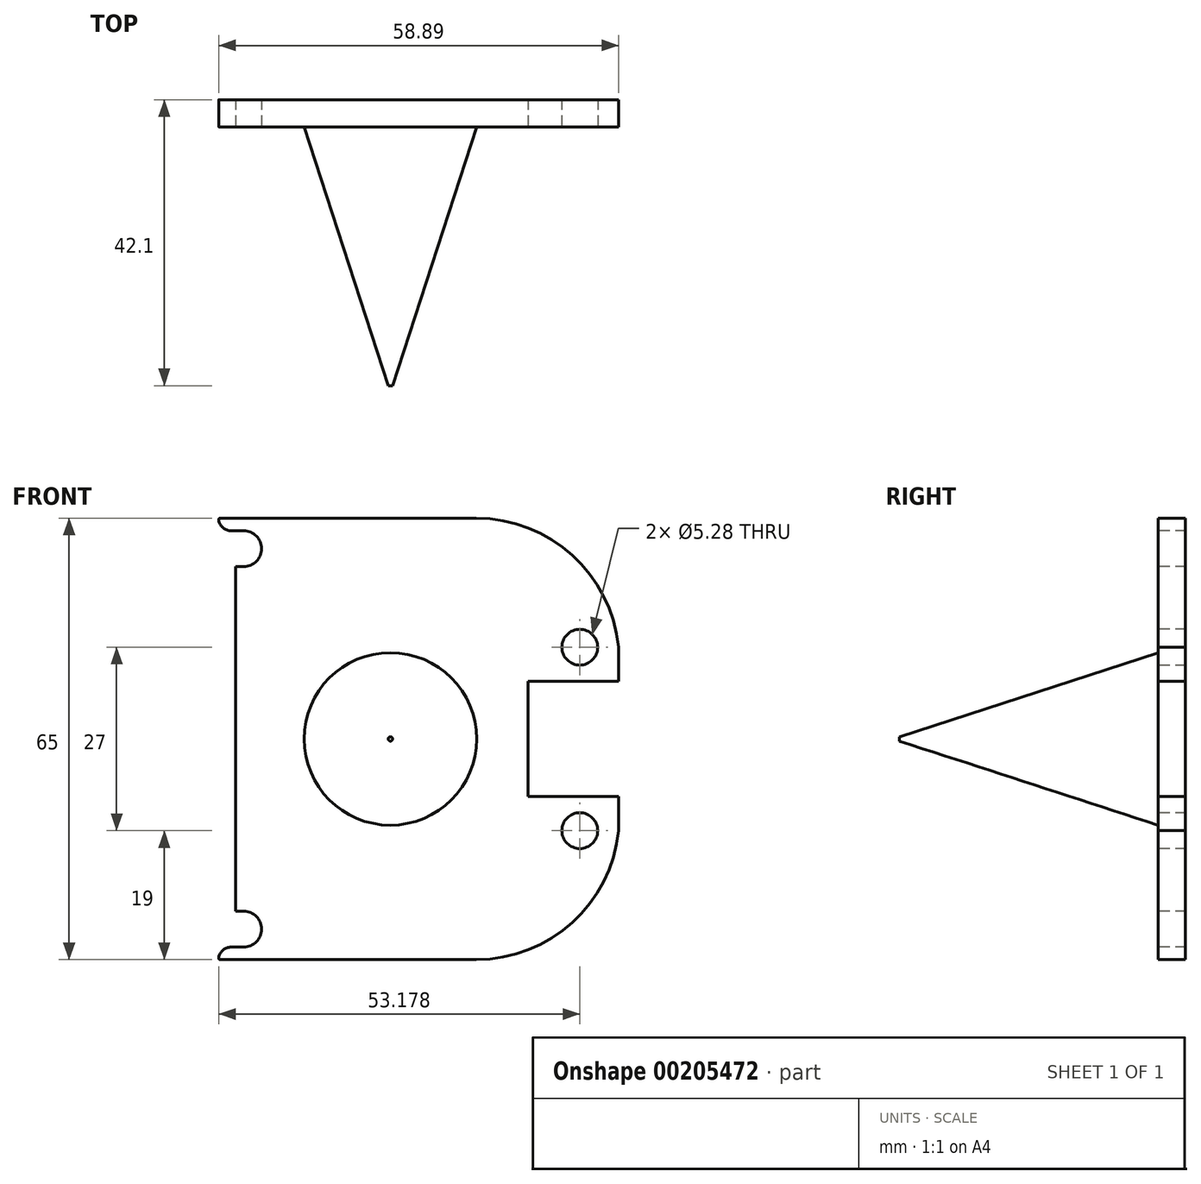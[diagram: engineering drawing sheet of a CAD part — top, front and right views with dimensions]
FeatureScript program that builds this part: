
annotation { "Feature Type Name" : "Feature", "Feature Type Description" : "" }
export const myFeature = defineFeature(function(context is Context, id is Id, definition is map)
    precondition{}
    {
        {
            var Q0;
            Q0=qCreatedBy(makeId("Front.planeOp"),FACE);
            var sketch = newSketch(context, id + "F0", { "sketchPlane" : qUnion([Q0])});
            skLineSegment(sketch, "E0.bottom", {"start": v(34.26, 37.43) * mm, "end": v(-34.26, 37.43) * mm});
            skLineSegment(sketch, "E0.top", {"start": v(34.26, -37.43) * mm, "end": v(-34.26, -37.43) * mm});
            skLineSegment(sketch, "E0.left", {"start": v(34.26, 37.43) * mm, "end": v(34.26, -37.43) * mm});
            skLineSegment(sketch, "E0.right", {"start": v(-34.26, 37.43) * mm, "end": v(-34.26, -37.43) * mm});
            skPoint(sketch, "E0.middle", {"position": v(0, 0) * mm});
            skSolve(sketch);
        }
        {
            var Q0;
            Q0=makeQuery(id+"F0.imprint","IMPRINT",FACE,{"disambiguationData":[TD([[makeQuery(id+"F0.imprint","IMPRINT",EDGE,{"derivedFrom":sQuery(id+"F0.wireOp",EDGE,"E0.bottom")}),1.0]])]});
            extrude(context, id + "F1", {"entities" : qUnion([Q0]), "depth" : 4 * mm});
        }
        {
            var Q0;
            Q0=makeQuery(id+"F1.opExtrude","CAP_FACE",FACE,{"disambiguationData":[OSD([sQuery(id+"F0.wireOp",EDGE,"E0.bottom"),sQuery(id+"F0.wireOp",EDGE,"E0.top"),sQuery(id+"F0.wireOp",EDGE,"E0.left"),sQuery(id+"F0.wireOp",EDGE,"E0.right")])],"isStart":false});
            var sketch = newSketch(context, id + "F2", { "sketchPlane" : qUnion([Q0])});
            skCircle(sketch, "E1", {"center": v(-34.26, 28) * mm, "radius": 2.64 * mm});
            skCircle(sketch, "E2", {"center": v(15.24, 13.5) * mm, "radius": 2.64 * mm});
            skLineSegment(sketch, "E3", {"start": v(-34.26, 0) * mm, "end": v(34.26, 0) * mm, "construction": true});
            skCircle(sketch, "E4.MirrorC", {"center": v(-34.26, -28) * mm, "radius": 2.64 * mm});
            skCircle(sketch, "E5.MirrorC", {"center": v(15.24, -13.5) * mm, "radius": 2.64 * mm});
            skLineSegment(sketch, "E6.bottom", {"start": v(7.64, 8.5) * mm, "end": v(20.95, 8.5) * mm});
            skLineSegment(sketch, "E7", {"start": v(-34.26, 32.5) * mm, "end": v(0, 32.5) * mm});
            skArc(sketch, "E8", {"start": v(0, 32.5) * mm, "mid": v(14.14, 27.04) * mm, "end": v(20.95, 13.5) * mm});
            skPoint(sketch, "E8.endSnap0", {"position": v(20.95, 8.5) * mm});
            skLineSegment(sketch, "E9", {"start": v(20.95, 13.5) * mm, "end": v(20.95, 8.5) * mm});
            skLineSegment(sketch, "E10", {"start": v(-34.26, 32.5) * mm, "end": v(-34.26, 37.43) * mm});
            skLineSegment(sketch, "E11", {"start": v(-34.26, 37.43) * mm, "end": v(34.26, 37.43) * mm});
            skLineSegment(sketch, "E12", {"start": v(34.26, 37.43) * mm, "end": v(34.26, 8.5) * mm});
            skLineSegment(sketch, "E13", {"start": v(7.64, 8.5) * mm, "end": v(7.64, 0) * mm});
            skLineSegment(sketch, "E14", {"start": v(7.64, 0) * mm, "end": v(34.26, 0) * mm});
            skLineSegment(sketch, "E15", {"start": v(34.26, 8.5) * mm, "end": v(34.26, 0) * mm});
            skLineSegment(sketch, "E16.MirrorCS", {"start": v(7.64, -8.5) * mm, "end": v(7.64, 0) * mm});
            skLineSegment(sketch, "E17.MirrorCS", {"start": v(7.64, -8.5) * mm, "end": v(20.95, -8.5) * mm});
            skLineSegment(sketch, "E18.MirrorCS", {"start": v(20.95, -13.5) * mm, "end": v(20.95, -8.5) * mm});
            skArc(sketch, "E19.MirrorCS", {"start": v(0, -32.5) * mm, "mid": v(14.14, -27.04) * mm, "end": v(20.95, -13.5) * mm});
            skLineSegment(sketch, "E20.MirrorCS", {"start": v(-34.26, -32.5) * mm, "end": v(0, -32.5) * mm});
            skLineSegment(sketch, "E21.MirrorCS", {"start": v(-34.26, -32.5) * mm, "end": v(-34.26, -37.43) * mm});
            skLineSegment(sketch, "E22.MirrorCS", {"start": v(-34.26, -37.43) * mm, "end": v(34.26, -37.43) * mm});
            skLineSegment(sketch, "E23.MirrorCS", {"start": v(34.26, -37.43) * mm, "end": v(34.26, -8.5) * mm});
            skLineSegment(sketch, "E24.MirrorCS", {"start": v(34.26, -8.5) * mm, "end": v(34.26, 0) * mm});
            skSolve(sketch);
        }
        {
            var Q0;
            Q0=qSketchRegion(id+"F2",true);
            extrude(context, id + "F3", {"entities" : qUnion([Q0]), "operationType" : NewBodyOperationType.REMOVE, "endBound" : BoundingType.THROUGH_ALL, "oppositeDirection" : true, "depth" : 25.4 * mm});
        }
        {
            var Q0;
            Q0=makeQuery(id+"F1.opExtrude","CAP_FACE",FACE,{"disambiguationData":[OSD([sQuery(id+"F0.wireOp",EDGE,"E0.bottom"),sQuery(id+"F0.wireOp",EDGE,"E0.top"),sQuery(id+"F0.wireOp",EDGE,"E0.left"),sQuery(id+"F0.wireOp",EDGE,"E0.right")])],"isStart":false});
            var sketch = newSketch(context, id + "F4", { "sketchPlane" : qUnion([Q0])});
            skLineSegment(sketch, "E25.bottom", {"start": v(-34.26, 25.36) * mm, "end": v(-35.46, 25.36) * mm});
            skLineSegment(sketch, "E25.top", {"start": v(-34.26, -25.36) * mm, "end": v(-35.46, -25.36) * mm});
            skLineSegment(sketch, "E25.left", {"start": v(-34.26, 25.36) * mm, "end": v(-34.26, -25.36) * mm});
            skLineSegment(sketch, "E25.right", {"start": v(-35.46, 25.36) * mm, "end": v(-35.46, -25.36) * mm});
            skLineSegment(sketch, "E26", {"start": v(-34.26, 30.64) * mm, "end": v(-36.06, 30.64) * mm});
            skArc(sketch, "E27", {"start": v(-36.06, 30.64) * mm, "mid": v(-37.4, 31.18) * mm, "end": v(-37.97, 32.5) * mm});
            skLineSegment(sketch, "E28", {"start": v(-37.97, 32.5) * mm, "end": v(-34.26, 32.5) * mm});
            skLineSegment(sketch, "E29", {"start": v(-35.46, 0) * mm, "end": v(0, 0) * mm, "construction": true});
            skArc(sketch, "E30.MirrorCS", {"start": v(-36.06, -30.64) * mm, "mid": v(-37.4, -31.18) * mm, "end": v(-37.97, -32.5) * mm});
            skLineSegment(sketch, "E31.MirrorCS", {"start": v(-34.26, -30.64) * mm, "end": v(-36.06, -30.64) * mm});
            skLineSegment(sketch, "E32.MirrorCS", {"start": v(-37.97, -32.5) * mm, "end": v(-34.26, -32.5) * mm});
            skSolve(sketch);
        }
        {
            var Q0;
            Q0=makeQuery(id+"F4.imprint","IMPRINT",FACE,{"disambiguationData":[TD([[makeQuery(id+"F4.imprint","IMPRINT",EDGE,{"derivedFrom":sQuery(id+"F4.wireOp",EDGE,"E30.MirrorCS")}),1.0]])]});
            var Q1;
            Q1=makeQuery(id+"F4.imprint","IMPRINT",FACE,{"disambiguationData":[TD([[makeQuery(id+"F4.imprint","IMPRINT",EDGE,{"derivedFrom":sQuery(id+"F4.wireOp",EDGE,"E25.bottom")}),1.0]])]});
            var Q2;
            Q2=makeQuery(id+"F4.imprint","IMPRINT",FACE,{"disambiguationData":[TD([[makeQuery(id+"F4.imprint","IMPRINT",EDGE,{"derivedFrom":sQuery(id+"F4.wireOp",EDGE,"E26")}),-1.0]])]});
            var Q3;
            Q3=makeQuery(id+"F1.opExtrude","CAP_FACE",FACE,{"disambiguationData":[OSD([sQuery(id+"F0.wireOp",EDGE,"E0.bottom"),sQuery(id+"F0.wireOp",EDGE,"E0.top"),sQuery(id+"F0.wireOp",EDGE,"E0.left"),sQuery(id+"F0.wireOp",EDGE,"E0.right")])],"isStart":true});
            extrude(context, id + "F5", {"entities" : qUnion([Q0, Q1, Q2]), "operationType" : NewBodyOperationType.ADD, "endBound" : BoundingType.UP_TO_SURFACE, "oppositeDirection" : true, "endBoundEntityFace" : qUnion([Q3]), "depth" : 25.4 * mm});
        }
        {
            var Q0;
            Q0=makeQuery(id+"F5.opExtrude","SWEPT_EDGE",EDGE,{"disambiguationData":[OSD([sQuery(id+"F4.wireOp",EDGE,"E30.MirrorCS"),sQuery(id+"F4.wireOp",EDGE,"E32.MirrorCS")])]});
            var Q1;
            Q1=makeQuery(id+"F5.opExtrude","SWEPT_EDGE",EDGE,{"disambiguationData":[OSD([sQuery(id+"F4.wireOp",EDGE,"E27"),sQuery(id+"F4.wireOp",EDGE,"E28")])]});
            fillet(context, id + "F6", {"entities" : qUnion([Q0, Q1]), "radius" : 0.25 * mm, "allowEdgeOverflow" : false});
        }
        {
            var Q0;
            Q0=makeQuery(id+"F2.imprint","IMPRINT",FACE,{"disambiguationData":[TD([[makeQuery(id+"F2.imprint","IMPRINT",EDGE,{"derivedFrom":sQuery(id+"F2.wireOp",EDGE,"E6.bottom")}),-1.0]])]});
            var sketch = newSketch(context, id + "F7", { "sketchPlane" : qUnion([Q0])});
            skCircle(sketch, "E33", {"center": v(-12.65, 0) * mm, "radius": 12.7 * mm});
            skSolve(sketch);
        }
        {
            var Q0;
            Q0=makeQuery(id+"F7.imprint","IMPRINT",FACE,{"disambiguationData":[TD([[makeQuery(id+"F7.imprint","IMPRINT",EDGE,{"derivedFrom":sQuery(id+"F7.wireOp",EDGE,"E33")}),1.0]])]});
            extrude(context, id + "F8", {"entities" : qUnion([Q0]), "operationType" : NewBodyOperationType.ADD, "depth" : 38.1 * mm, "hasDraft" : true, "draftAngle" : 18 * degree, "draftPullDirection" : true});
        }
    });
